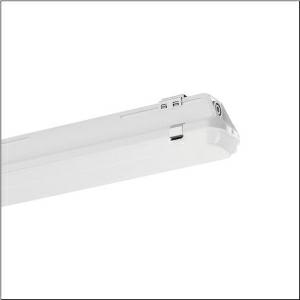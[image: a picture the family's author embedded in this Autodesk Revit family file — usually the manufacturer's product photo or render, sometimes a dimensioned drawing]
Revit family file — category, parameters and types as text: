
# Revit family: monsun_21_51fb10dp360b
name_source: partatom
category: Lighting Fixtures
units: mm (PartAtom-declared; Revit-internal decimal feet)

## family parameters
Cut with Voids When Loaded = No
Host = Face
Light Source = No
Part Type = Normal
Room Calculation Point = No
Round Connector Dimension = Use Diameter
Shared = No

## types (1)
- --- (1 x LED, 6060 lm, 43.2 W, 3000K)
    Apparent Load = 43 VA
    CIE Flux Codes = 47 77 93 94 100
    Color Rendering = 80
    Color Temperature = 3000K
    Default Elevation = 1800 mm
    Description = Monsun 21, damp-proof luminaire, chain hanger, primary optical cover: enclosure, of PMMA, light emission: direct distribution, primary light characteristic: symmetric, installation type: suspended mounting, surface-mounted, horizontal mounting, vertical mounting, LED, rated luminous flux: 6.060lm, luminous efficacy: 154lm/W, light colour: 830, colour temperature: 3000K, control gear: DALI 2, with terminal, 5-pole, max. 2.5mm², mains connection: 220..240V, AC, 50/60Hz, rated input power: 39W, housing, of glass-fibre reinforced polyester, uncoated, bright grey, incl. chain hanger, length: 1.590mm, width: 90mm, height: 88mm, clip for enclosure, of stainless steel (V2A), ceiling mounting element, of stainless steel (V2A), chain hanger, of stainless steel (V2A), protection rating (complete): IP66, insulation class (complete): insulation class I (protective earthing), certification: CE, ENEC, VDE, UKCA, protection symbol: D, impact resistance: IK04, permissible operating ambient temperature: -25..+35°C, standard: EN 50419, EN 60598-2-1, corresponds to IFS (International Featured Standards) requirements for safety and quality in the food industry, for indoor or canopied outdoor use, no direct snow, no direct sun, no direct rain, contact your sales advisor before using the luminaires in applications with unclear chemical exposure, large temperature fluctuations or condensation-forming humidity, LABS conformity tested according to VDMA 24364:2018-05, packaging unit: 1 piece
    Height = 89 mm
    Lamp = 1 x LED
    Lamp Light Flux = 6060 lm
    Lamp Power = 43.2 W
    Lamp count = 1
    Length = 1590 mm
    Luminous efficacy = 140 lm/W
    Manufacturer = Siteco
    ModVariant = No
    Model = 51FB10DP360B
    Mounting Place = Ceiling
    Mounting Type = Surface mounted
    Number of Poles = 1
    OnlyDefault = Yes
    Power Factor = 1
    Product Name = Monsun 21
    Product group = damp-proof luminaire
    ProductGroupID = 300
    Protection Class = Protection class I
    Protection Degree = IP 66
    RLX_Detail_Level = 1
    RLX_Emergency_Light_Flux = 0 lm
    RLX_Emergency_Type = 0
    RLX_Emergency_Type_DB = No
    RlxData = <blob elided: 92325 chars, md5=beb288da>
    Socket = socket
    Standby Power = 0 W
    System Light Flux = 6060 lm
    System Power = 43 W
    Type Comments = factory setting: luminous flux: 100 % | dim-lin: 254 | 286 mA
    Type Image = l_1319656.jpg
    URL = http://relux.com
    VarID = @adj_146271
    Voltage = 0 V
    Weight = 0.00 kg
    Width = 90 mm

## geometry (parser evidence)
native form markers: Blend x4, Sweep x15
no freeform markers — native parametric forms only
